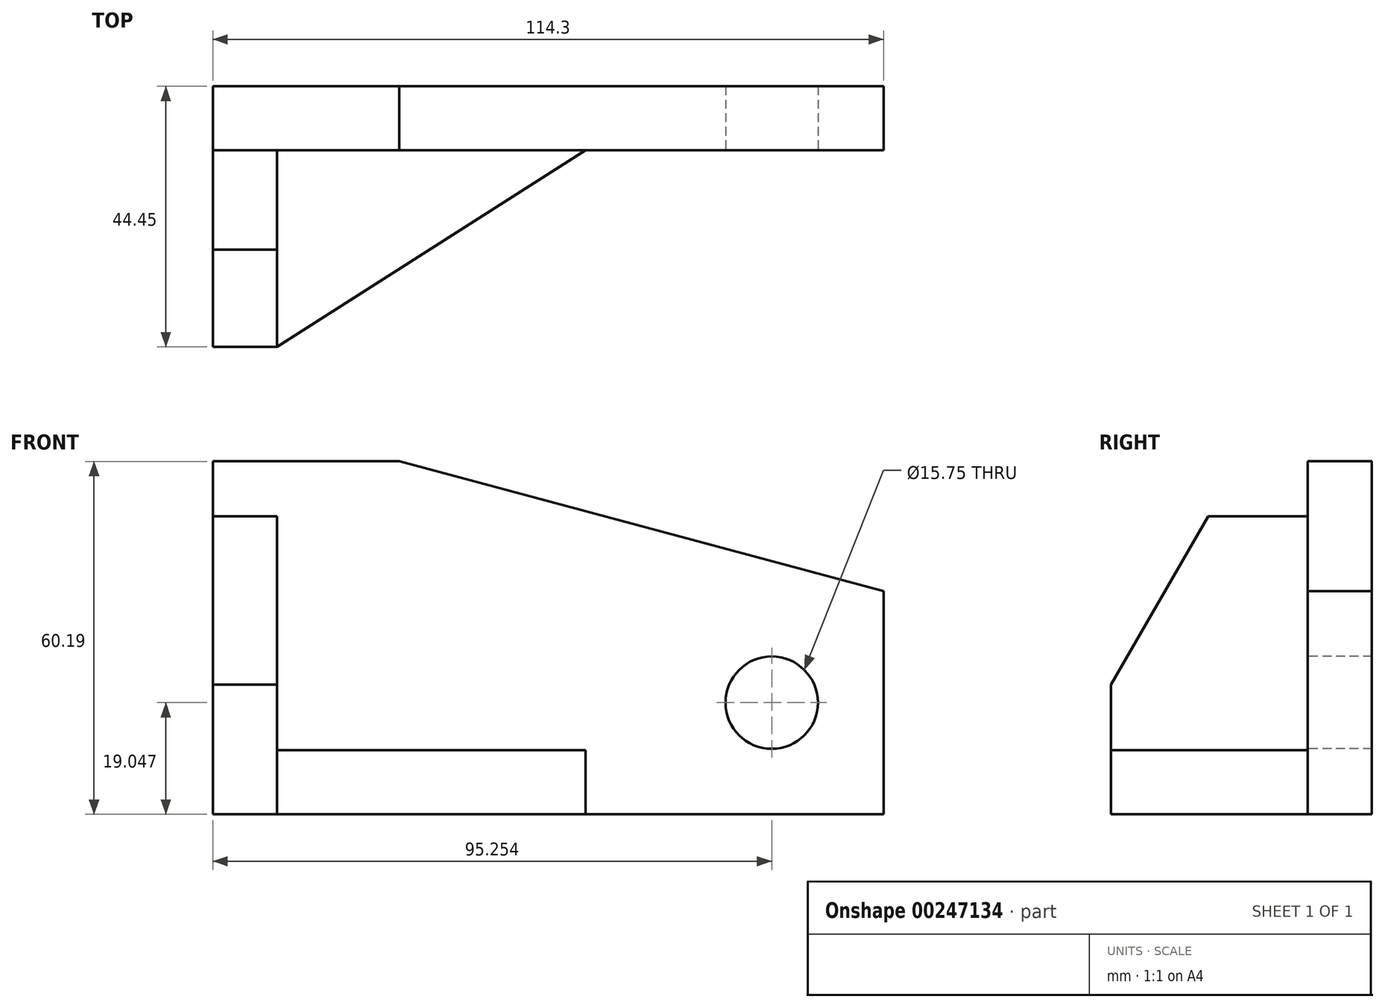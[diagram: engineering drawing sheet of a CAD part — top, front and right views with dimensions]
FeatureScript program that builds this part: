
annotation { "Feature Type Name" : "Feature", "Feature Type Description" : "" }
export const myFeature = defineFeature(function(context is Context, id is Id, definition is map)
    precondition{}
    {
        {
            var Q0;
            Q0=qCreatedBy(makeId("Front.planeOp"),FACE);
            var sketch = newSketch(context, id + "F0", { "sketchPlane" : qUnion([Q0])});
            skLineSegment(sketch, "E0.bottom", {"start": v(-53.2, 53.58) * mm, "end": v(-21.46, 53.58) * mm});
            skLineSegment(sketch, "E0.top", {"start": v(-53.2, -6.61) * mm, "end": v(61.1, -6.61) * mm});
            skLineSegment(sketch, "E0.left", {"start": v(-53.2, 53.58) * mm, "end": v(-53.2, -6.61) * mm});
            skLineSegment(sketch, "E0.right", {"start": v(61.1, 31.47) * mm, "end": v(61.1, -6.61) * mm});
            skLineSegment(sketch, "E1", {"start": v(-21.46, 53.58) * mm, "end": v(61.1, 31.47) * mm});
            skCircle(sketch, "E2", {"center": v(42.04, 12.44) * mm, "radius": 7.87 * mm});
            skLineSegment(sketch, "E3.bottom", {"start": v(-53.2, 44.19) * mm, "end": v(-42.28, 44.19) * mm});
            skLineSegment(sketch, "E3.right", {"start": v(-42.28, 44.19) * mm, "end": v(-42.28, -6.61) * mm});
            skLineSegment(sketch, "E4.bottom", {"start": v(-42.28, 4.3) * mm, "end": v(10.3, 4.3) * mm});
            skLineSegment(sketch, "E4.right", {"start": v(10.3, 4.3) * mm, "end": v(10.3, -6.61) * mm});
            skSolve(sketch);
        }
        {
            var Q0;
            Q0=makeQuery(id+"F0.imprint","IMPRINT",FACE,{"disambiguationData":[TD([[makeQuery(id+"F0.imprint","IMPRINT",EDGE,{"derivedFrom":sQuery(id+"F0.wireOp",EDGE,"E3.bottom")}),-1.0]])]});
            var Q1;
            Q1=makeQuery(id+"F0.imprint","IMPRINT",FACE,{"disambiguationData":[TD([[makeQuery(id+"F0.imprint","IMPRINT",EDGE,{"derivedFrom":sQuery(id+"F0.wireOp",EDGE,"E4.bottom")}),-1.0]])]});
            var Q2;
            {var subQ1=sQuery(id+"F0.wireOp",EDGE,"E0.top");Q2=makeQuery(id+"F0.imprint","IMPRINT",FACE,{"disambiguationData":[TD([[makeQuery(id+"F0.imprint","IMPRINT",EDGE,{"derivedFrom":subQ1}),1.0]])]});}
            extrude(context, id + "F1", {"entities" : qUnion([Q0, Q1, Q2]), "oppositeDirection" : true, "depth" : 10.92 * mm});
        }
        {
            var Q0;
            Q0=makeQuery(id+"F0.imprint","IMPRINT",FACE,{"disambiguationData":[TD([[makeQuery(id+"F0.imprint","IMPRINT",EDGE,{"derivedFrom":sQuery(id+"F0.wireOp",EDGE,"E3.bottom")}),-1.0]])]});
            var Q1;
            Q1=makeQuery(id+"F0.imprint","IMPRINT",FACE,{"disambiguationData":[TD([[makeQuery(id+"F0.imprint","IMPRINT",EDGE,{"derivedFrom":sQuery(id+"F0.wireOp",EDGE,"E4.bottom")}),-1.0]])]});
            extrude(context, id + "F2", {"entities" : qUnion([Q0, Q1]), "operationType" : NewBodyOperationType.ADD, "depth" : 33.53 * mm});
        }
        {
            var Q0;
            Q0=makeQuery(id+"F2.opExtrude","SWEPT_FACE",FACE,{"disambiguationData":[OSD([sQuery(id+"F0.wireOp",EDGE,"E3.right")])]});
            var sketch = newSketch(context, id + "F3", { "sketchPlane" : qUnion([Q0])});
            skLineSegment(sketch, "E5", {"start": v(-33.53, 15.48) * mm, "end": v(-16.96, 44.19) * mm});
            skPoint(sketch, "E6", {"position": v(-11.3, 44.19) * mm});
            skSolve(sketch);
        }
        {
            var Q0;
            Q0 = qSketchRegion(id + "F3", true);
            var Q1;
            {var subQ0=sQuery(id+"F3.wireOp",EDGE,"E5");Q1=makeQuery(id+"F3.imprint","IMPRINT",FACE,{"disambiguationData":[TD([[makeQuery(id+"F3.imprint","IMPRINT",EDGE,{"derivedFrom":subQ0}),1.0]])]});}
            extrude(context, id + "F4", {"entities" : qUnion([Q0, Q1]), "operationType" : NewBodyOperationType.REMOVE, "oppositeDirection" : true, "depth" : 25.4 * mm});
        }
        {
            var Q0;
            Q0=makeQuery(id+"F2.opExtrude","SWEPT_FACE",FACE,{"disambiguationData":[OSD([sQuery(id+"F0.wireOp",EDGE,"E4.bottom")])]});
            var sketch = newSketch(context, id + "F5", { "sketchPlane" : qUnion([Q0])});
            skLineSegment(sketch, "E7", {"start": v(-42.28, -33.53) * mm, "end": v(10.3, 0) * mm});
            skLineSegment(sketch, "E8", {"start": v(10.3, 10.92) * mm, "end": v(10.3, 0) * mm, "construction": true});
            skSolve(sketch);
        }
        {
            var Q0;
            Q0=makeQuery(id+"F5.imprint","IMPRINT",FACE,{"disambiguationData":[TD([[makeQuery(id+"F5.imprint","IMPRINT",EDGE,{"derivedFrom":sQuery(id+"F5.wireOp",EDGE,"E7")}),-1.0]])]});
            extrude(context, id + "F6", {"entities" : qUnion([Q0]), "operationType" : NewBodyOperationType.REMOVE, "oppositeDirection" : true, "depth" : 25.4 * mm});
        }
        {
            var Q0;
            {var subQ3=sQuery(id+"F0.wireOp",EDGE,"E0.bottom");Q0=makeQuery(id+"F0.imprint","IMPRINT",FACE,{"disambiguationData":[TD([[makeQuery(id+"F0.imprint","IMPRINT",EDGE,{"derivedFrom":subQ3}),-1.0]])]});}
            extrude(context, id + "F7", {"entities" : qUnion([Q0]), "operationType" : NewBodyOperationType.ADD, "oppositeDirection" : true, "depth" : 10.92 * mm});
        }
    });
